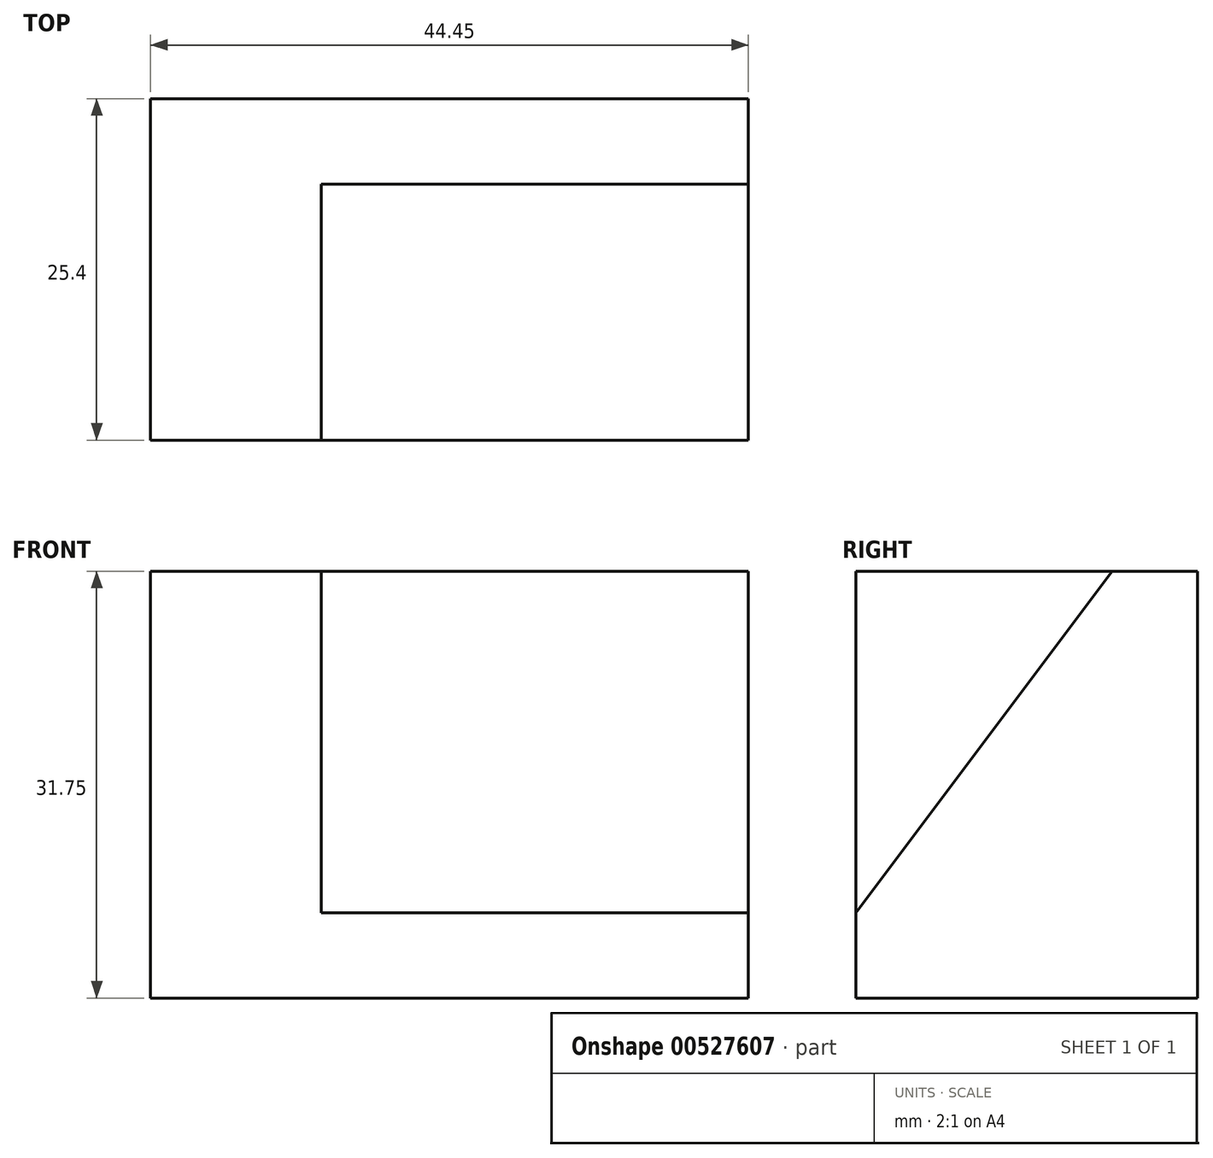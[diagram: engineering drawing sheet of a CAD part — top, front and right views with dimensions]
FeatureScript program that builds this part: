
annotation { "Feature Type Name" : "Feature", "Feature Type Description" : "" }
export const myFeature = defineFeature(function(context is Context, id is Id, definition is map)
    precondition{}
    {
        {
            var Q0;
            Q0=qCreatedBy(makeId("Right.planeOp"),FACE);
            var sketch = newSketch(context, id + "F0", { "sketchPlane" : qUnion([Q0])});
            skLineSegment(sketch, "E0", {"start": v(0, 0) * mm, "end": v(0, 6.35) * mm});
            skLineSegment(sketch, "E1", {"start": v(0, 6.35) * mm, "end": v(19.05, 31.75) * mm});
            skLineSegment(sketch, "E2", {"start": v(19.05, 31.75) * mm, "end": v(25.4, 31.75) * mm});
            skLineSegment(sketch, "E3", {"start": v(25.4, 31.75) * mm, "end": v(25.4, 0) * mm});
            skLineSegment(sketch, "E4", {"start": v(25.4, 0) * mm, "end": v(0, 0) * mm});
            skSolve(sketch);
        }
        {
            var Q0;
            Q0=makeQuery(id+"F0.imprint","IMPRINT",FACE,{"disambiguationData":[TD([[makeQuery(id+"F0.imprint","IMPRINT",EDGE,{"derivedFrom":sQuery(id+"F0.wireOp",EDGE,"E0")}),-1.0]])]});
            extrude(context, id + "F1", {"entities" : qUnion([Q0]), "depth" : 31.75 * mm, "offsetDistance" : 25.4 * mm});
        }
        {
            var Q0;
            Q0=qCreatedBy(makeId("Right.planeOp"),FACE);
            var sketch = newSketch(context, id + "F2", { "sketchPlane" : qUnion([Q0])});
            skLineSegment(sketch, "E5", {"start": v(25.4, 0) * mm, "end": v(25.4, 31.75) * mm});
            skLineSegment(sketch, "E6", {"start": v(25.4, 31.75) * mm, "end": v(17.97, 31.75) * mm});
            skLineSegment(sketch, "E7", {"start": v(17.97, 31.75) * mm, "end": v(0, 31.75) * mm});
            skLineSegment(sketch, "E8", {"start": v(0, 31.75) * mm, "end": v(0, 0) * mm});
            skLineSegment(sketch, "E9", {"start": v(0, 0) * mm, "end": v(25.4, 0) * mm});
            skSolve(sketch);
        }
        {
            var Q0;
            Q0 = qSketchRegion(id + "F2", true);
            extrude(context, id + "F3", {"entities" : qUnion([Q0]), "operationType" : NewBodyOperationType.ADD, "oppositeDirection" : true, "depth" : 12.7 * mm, "offsetDistance" : 25.4 * mm});
        }
    });
